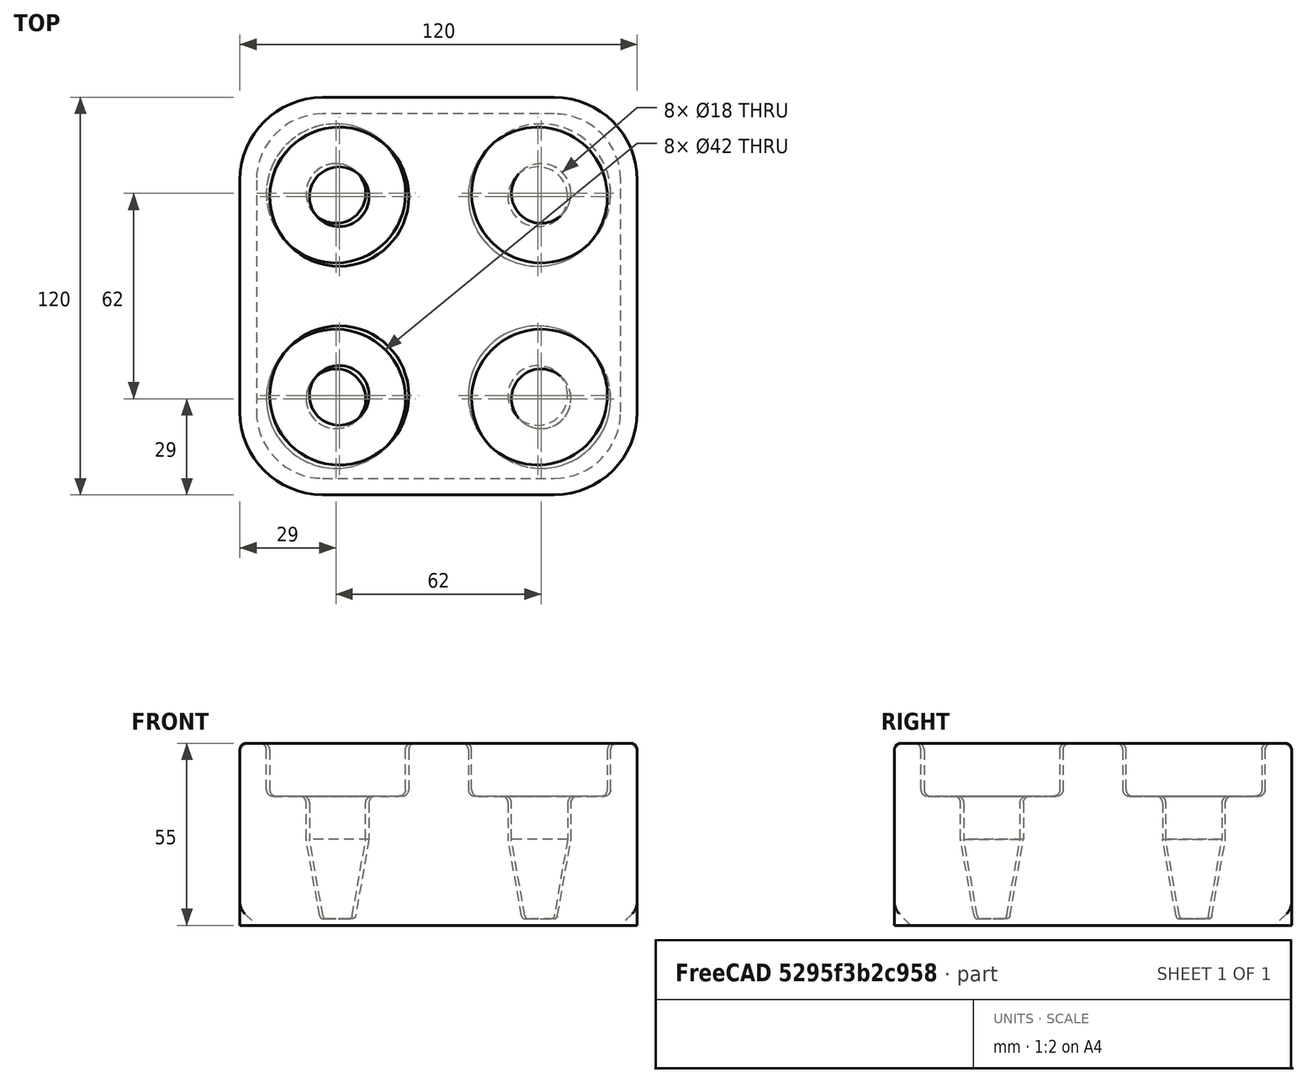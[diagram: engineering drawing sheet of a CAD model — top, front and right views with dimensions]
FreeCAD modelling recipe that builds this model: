
FCSTD DOCUMENT  (FreeCAD 1.0R39285 (Git))
Label: DressingBottleHolder
License: All rights reserved
LicenseURL: https://en.wikipedia.org/wiki/All_rights_reserved
objects: TechDraw::DrawViewDimension×16, Sketcher::SketchObject×7, Part::Part2DObjectPython×4, PartDesign::Body×3, Part::Feature×1, PartDesign::Pad×1, PartDesign::Groove×1, PartDesign::PolarPattern×1, PartDesign::Fillet×1, TechDraw::DrawSVGTemplate×1, TechDraw::DrawProjGroupItem×1, TechDraw::DrawProjGroup×1, TechDraw::DrawComplexSection×1, TechDraw::DrawPage×1
note: 57 computed .brp shape members not serialized (recipe doc carries the construction recipe); baked Part::Feature solids carry a one-line shape summary decoded from their .brp

FEATURE [Part::Feature] Part__Feature  label="2X2 step"
  shape: bbox 124.1 x 124.1 x 55 mm, 70 faces (baked)
FEATURE [Sketcher::SketchObject] Sketch
  ArcFitTolerance = 1e-06
  AttachmentSupport = -> [XY_Plane]
  FullyConstrained = true
  MakeInternals = false
  MapMode = 5
  sketch-geometry (11):
    g0: LineSegment StartX=-60 StartY=35 StartZ=0 EndX=-60 EndY=-35 EndZ=0
    g1: LineSegment StartX=-35 StartY=-60 StartZ=0 EndX=35 EndY=-60 EndZ=0
    g2: LineSegment StartX=60 StartY=-35 StartZ=0 EndX=60 EndY=35 EndZ=0
    g3: LineSegment StartX=35 StartY=60 StartZ=0 EndX=-35 EndY=60 EndZ=0
    g4: ArcOfCircle CenterX=-35 CenterY=35 CenterZ=0 NormalX=0 NormalY=0 NormalZ=1 AngleXU=0 Radius=25 StartAngle=1.5708 EndAngle=3.14159
    g5: ArcOfCircle CenterX=-35 CenterY=-35 CenterZ=0 NormalX=0 NormalY=0 NormalZ=1 AngleXU=0 Radius=25 StartAngle=3.14159 EndAngle=4.71239
    g6: ArcOfCircle CenterX=35 CenterY=-35 CenterZ=0 NormalX=0 NormalY=0 NormalZ=1 AngleXU=0 Radius=25 StartAngle=4.71239 EndAngle=6.28319
    g7: ArcOfCircle CenterX=35 CenterY=35 CenterZ=0 NormalX=0 NormalY=0 NormalZ=1 AngleXU=0 Radius=25 StartAngle=-5.0129e-12 EndAngle=1.5708
    g8: GeomPoint [constr] X=-60 Y=60 Z=0
    g9: GeomPoint [constr] X=60 Y=-60 Z=0
    g10: Circle [constr] CenterX=31 CenterY=31 CenterZ=0 NormalX=0 NormalY=0 NormalZ=1 AngleXU=0 Radius=23
  constraints (25):
    c: Tangent(g0,g4) = -1.5708
    c: Tangent(g0,g5) = -1.5708
    c: Tangent(g1,g5) = -1.5708
    c: Tangent(g1,g6) = -1.5708
    c: Tangent(g2,g6) = -1.5708
    c: Tangent(g2,g7) = -1.5708
    c: Tangent(g3,g7) = -1.5708
    c: Tangent(g3,g4) = -1.5708
    c: Vertical(g0)
    c: Vertical(g2)
    c: Horizontal(g1)
    c: Horizontal(g3)
    c: Equal(g6,g7)
    c: PointOnObject(g8,g0)
    c: PointOnObject(g8,g3)
    c: PointOnObject(g9,g1)
    c: PointOnObject(g9,g2)
    c: Symmetric(g2,g0,g-2)
    c: Symmetric(g1,g3,g-1)
    c: Equal(g0,g3)
    c: DistanceY(g1,g3) = 120
    c: Radius(g7) = 25
    c: DistanceX(g10) = 31
    c: DistanceY(g10) = 31
    c: Diameter(g10) = 46
FEATURE [PartDesign::Pad] Pad
  Direction = (0,0,1)
  Length = 55
  Length2 = 10
  Profile = -> Sketch
  ReferenceAxis = -> Sketch [N_Axis]
  Refine = true
  Suppressed = false
  Type = 0
FEATURE [Sketcher::SketchObject] Sketch001
  ArcFitTolerance = 1e-06
  AttachmentOffset = pos=(31,0,-31) rot=(0,0,1;0rad)
  AttachmentSupport = -> [XZ_Plane]
  ExternalGeometry = -> [Pad]
  FullyConstrained = true
  MakeInternals = false
  MapMode = 5
  Placement = pos=(31,31,-6.9e-15) rot=(1,0,0;1.5708rad)
  expr: Constraints[29] = 2 mm
  expr: Constraints[38] = 26 mm
  sketch-geometry (16):
    g0: LineSegment StartX=0 StartY=55 StartZ=0 EndX=0 EndY=2 EndZ=0
    g1: LineSegment StartX=0 StartY=2 StartZ=0 EndX=3.91552 EndY=2 EndZ=0
    g2: LineSegment StartX=4.9 StartY=2.8245 StartZ=0 EndX=8.96896 EndY=25.649 EndZ=0
    g3: LineSegment StartX=9 StartY=26 StartZ=0 EndX=9 EndY=37 EndZ=0
    g4: LineSegment StartX=11 StartY=39 StartZ=0 EndX=19 EndY=39 EndZ=0
    g5: LineSegment StartX=21 StartY=41 StartZ=0 EndX=21 EndY=53 EndZ=0
    g6: LineSegment StartX=0 StartY=55 StartZ=0 EndX=23 EndY=55 EndZ=0
    g7: ArcOfCircle CenterX=23 CenterY=53 CenterZ=0 NormalX=0 NormalY=0 NormalZ=1 AngleXU=0 Radius=2 StartAngle=1.5708 EndAngle=3.14159
    g8: ArcOfCircle CenterX=19 CenterY=41 CenterZ=0 NormalX=0 NormalY=0 NormalZ=1 AngleXU=0 Radius=2 StartAngle=4.71239 EndAngle=6.28319
    g9: GeomPoint [constr] X=21 Y=39 Z=0
    g10: ArcOfCircle CenterX=11 CenterY=37 CenterZ=0 NormalX=0 NormalY=0 NormalZ=1 AngleXU=0 Radius=2 StartAngle=1.5708 EndAngle=3.14159
    g11: GeomPoint [constr] X=9 Y=39 Z=0
    g12: ArcOfCircle CenterX=7 CenterY=26 CenterZ=0 NormalX=0 NormalY=0 NormalZ=1 AngleXU=0 Radius=2 StartAngle=6.10677 EndAngle=6.28319
    g13: GeomPoint [constr] X=9 Y=25.8231 Z=0
    g14: ArcOfCircle CenterX=3.91552 CenterY=3 CenterZ=0 NormalX=0 NormalY=0 NormalZ=1 AngleXU=0 Radius=1 StartAngle=4.71239 EndAngle=6.10677
    g15: GeomPoint [constr] X=4.75302 Y=2 Z=0
  constraints (40):
    c: Vertical(g0)
    c: Coincident(g0,g1)
    c: Horizontal(g1)
    c: Vertical(g3)
    c: Horizontal(g4)
    c: Vertical(g5)
    c: Coincident(g0,g6)
    c: Horizontal(g6)
    c: Tangent(g7,g5) = 1.5708
    c: Tangent(g7,g6) = 1.5708
    c: PointOnObject(g9,g4)
    c: PointOnObject(g9,g5)
    c: Tangent(g4,g8) = -1.5708
    c: Tangent(g5,g8) = -1.5708
    c: PointOnObject(g11,g3)
    c: PointOnObject(g11,g4)
    c: Tangent(g3,g10) = 1.5708
    c: Tangent(g4,g10) = 1.5708
    c: PointOnObject(g13,g2)
    c: PointOnObject(g13,g3)
    c: Tangent(g2,g12) = -1.5708
    c: Tangent(g3,g12) = -1.5708
    c: PointOnObject(g15,g1)
    c: PointOnObject(g15,g2)
    c: Tangent(g1,g14) = -1.5708
    c: Tangent(g2,g14) = -1.5708
    c: Equal(g7,g8)
    c: Equal(g8,g10)
    c: Radius(g7) = 2
    c: DistanceY(g0) = 2
    c: Radius(g14) = 1
    c: DistanceY(g11) = 39
    c: PointOnObject(g6,g-3)
    c: DistanceX(g0,g5) = 21
    c: DistanceX(g0,g3) = 9
    c: DistanceX(g0,g2) = 4.9
    c: Equal(g12,g10)
    c: PointOnObject(g0,g-2)
    c: DistanceY(g3) = 26
    c: DistanceX(g6) = 23
FEATURE [PartDesign::Groove] Groove
  Angle = 360
  Angle2 = 60
  Axis = (0,2e-16,1)
  Base = (31,31,-6.9e-15)
  BaseFeature = -> Pad
  Profile = -> Sketch001
  ReferenceAxis = -> Sketch001 [V_Axis]
  Refine = true
  Suppressed = false
  Type = 0
FEATURE [PartDesign::PolarPattern] PolarPattern
  Angle = 360
  Axis = -> Z_Axis
  BaseFeature = -> Groove
  Mode = 0
  Occurrences = 4
  Offset = 120
  Originals = -> [Groove]
  Refine = true
  Suppressed = false
  TransformMode = 0
FEATURE [PartDesign::Fillet] Fillet
  Base = -> PolarPattern [Edge20]
  BaseFeature = -> PolarPattern
  Radius = 2
  Refine = true
  SupportTransform = false
  Suppressed = false
  UseAllEdges = false
FEATURE [TechDraw::DrawSVGTemplate] Template
  Height = 297
  Orientation = 0
  Template = <path>
  Width = 210
FEATURE [Sketcher::SketchObject] Sketch002
  ArcFitTolerance = 1e-06
  AttachmentSupport = -> [Fillet]
  FullyConstrained = false
  MakeInternals = false
  MapMode = 5
  Placement = pos=(0,0,55) rot=(0,0,1;0rad)
  sketch-geometry (3):
    g0: LineSegment StartX=-75.5453 StartY=0 StartZ=0 EndX=0 EndY=0 EndZ=0
    g1: LineSegment StartX=0 StartY=0 StartZ=0 EndX=0 EndY=31 EndZ=0
    g2: LineSegment StartX=0 StartY=31 StartZ=0 EndX=79.1188 EndY=31 EndZ=0
  constraints (7):
    c: PointOnObject(g0,g-1)
    c: Coincident(g0,g-1)
    c: Coincident(g0,g1)
    c: PointOnObject(g1,g-2)
    c: Coincident(g1,g2)
    c: Horizontal(g2)
    c: DistanceY(g1,g1) = 31
FEATURE [PartDesign::Body] Body  label="2x2"
  AllowCompound = false
  Group = -> [Sketch,Sketch001,Pad,Groove,PolarPattern,Fillet,Sketch002]
  Origin = -> Origin
  Tip = -> Fillet
FEATURE [TechDraw::DrawProjGroupItem] ProjItem  label="Top"
  CoarseView = false
  Direction = (0,0,1)
  Focus = 100
  HardHidden = false
  IsoCount = 0
  IsoHidden = false
  IsoVisible = false
  LockPosition = true
  Perspective = false
  Rotation = 0
  RotationVector = (1,0,0)
  ScaleType = 0
  ScrubCount = 1
  SeamHidden = false
  SeamVisible = false
  SmoothHidden = false
  SmoothVisible = true
  Source = -> [Body]
  Type = 0
  X = 0
  XDirection = (1,0,0)
  Y = 0
FEATURE [TechDraw::DrawProjGroup] ProjGroup
  Anchor = -> ProjItem
  AutoDistribute = true
  LockPosition = false
  ProjectionType = 0
  Rotation = 0
  ScaleType = 0
  Source = -> [Body]
  Views = -> [ProjItem]
  X = 110.819
  Y = 78.5207
  spacingX = 15
  spacingY = 15
FEATURE [TechDraw::DrawViewDimension] Dimension
  AngleOverride = false
  Arbitrary = false
  ArbitraryTolerances = false
  BoxCorners = (2) [(-60,-60,-1e-07),(60,60,1e-07)]
  EqualTolerance = true
  ExtensionAngle = 0
  FormatSpec = %.2w
  FormatSpecOverTolerance = %+.2w
  FormatSpecUnderTolerance = %+.2w
  Inverted = false
  LineAngle = 0
  LockPosition = false
  MeasureType = 1
  OverTolerance = 0
  References2D = -> [ProjItem]
  Rotation = 0
  ScaleType = 0
  TheoreticalExact = false
  Type = 1
  UnderTolerance = 0
  X = 0
  Y = 92.7629
FEATURE [TechDraw::DrawViewDimension] Dimension001
  AngleOverride = false
  Arbitrary = false
  ArbitraryTolerances = false
  BoxCorners = (2) [(-60,-60,-1e-07),(60,60,1e-07)]
  EqualTolerance = true
  ExtensionAngle = 0
  FormatSpec = %.2w
  FormatSpecOverTolerance = %+.2w
  FormatSpecUnderTolerance = %+.2w
  Inverted = false
  LineAngle = 0
  LockPosition = false
  MeasureType = 1
  OverTolerance = 0
  References2D = -> [ProjItem]
  Rotation = 0
  ScaleType = 0
  TheoreticalExact = false
  Type = 2
  UnderTolerance = 0
  X = -105.136
  Y = 0
FEATURE [TechDraw::DrawViewDimension] Dimension002
  AngleOverride = false
  Arbitrary = false
  ArbitraryTolerances = false
  BoxCorners = (2) [(-60,-60,-1e-07),(60,60,1e-07)]
  EqualTolerance = true
  ExtensionAngle = 0
  FormatSpec = R%.2w
  FormatSpecOverTolerance = %+.2w
  FormatSpecUnderTolerance = %+.2w
  Inverted = false
  LineAngle = 0
  LockPosition = false
  MeasureType = 1
  OverTolerance = 0
  References2D = -> [ProjItem]
  Rotation = 0
  ScaleType = 0
  TheoreticalExact = false
  Type = 4
  UnderTolerance = 0
  X = 70.8117
  Y = -52.3925
FEATURE [TechDraw::DrawComplexSection] ComplexSection  label="Section A - A"
  BaseView = -> ProjItem
  CoarseView = false
  CutSurfaceDisplay = 2
  CuttingToolWireObject = -> Sketch002
  Direction = (1e-16,-1,0)
  FileGeomPattern = <path>
  FileHatchPattern = <path>
  Focus = 100
  FuseBeforeCut = false
  HardHidden = false
  HatchOffset = (0,0,0)
  HatchRotation = 0
  HatchScale = 1
  IsoCount = 0
  IsoHidden = false
  IsoVisible = false
  LockPosition = false
  NameGeomPattern = Diamond
  Perspective = false
  ProjectionStrategy = 0
  Rotation = 0
  ScaleType = 0
  ScrubCount = 1
  SeamHidden = false
  SeamVisible = false
  SectionDirection = 4
  SectionLineStretch = 1
  SectionNormal = (1e-16,-1,0)
  SectionOrigin = (0,0,0)
  SectionSymbol = A
  SmoothHidden = false
  SmoothVisible = true
  Source = -> [Body]
  TrimAfterCut = false
  UsePreviousCut = false
  X = 110.819
  XDirection = (1,1e-16,0)
  Y = 208.194
FEATURE [TechDraw::DrawViewDimension] Dimension003
  AngleOverride = false
  Arbitrary = false
  ArbitraryTolerances = false
  BoxCorners = (2) [(-60,-27.5,-1e-07),(60,27.5,1e-07)]
  EqualTolerance = true
  ExtensionAngle = 0
  FormatSpec = %.2w
  FormatSpecOverTolerance = %+.2w
  FormatSpecUnderTolerance = %+.2w
  Inverted = false
  LineAngle = 0
  LockPosition = false
  MeasureType = 1
  OverTolerance = 0
  References2D = -> [ComplexSection]
  Rotation = 0
  ScaleType = 0
  TheoreticalExact = false
  Type = 2
  UnderTolerance = 0
  X = -76.9265
  Y = -30.5684
FEATURE [TechDraw::DrawViewDimension] Dimension005
  AngleOverride = false
  Arbitrary = false
  ArbitraryTolerances = false
  BoxCorners = (2) [(-60,-27.5,-1e-07),(60,27.5,1e-07)]
  EqualTolerance = true
  ExtensionAngle = 0
  FormatSpec = %.2w
  FormatSpecOverTolerance = %+.2w
  FormatSpecUnderTolerance = %+.2w
  Inverted = false
  LineAngle = 0
  LockPosition = false
  MeasureType = 1
  OverTolerance = 0
  References2D = -> [ComplexSection]
  Rotation = 0
  ScaleType = 0
  TheoreticalExact = false
  Type = 2
  UnderTolerance = 0
  X = -83.9265
  Y = 19.5
FEATURE [TechDraw::DrawViewDimension] Dimension006
  AngleOverride = false
  Arbitrary = false
  ArbitraryTolerances = false
  BoxCorners = (2) [(-60,-27.5,-1e-07),(60,27.5,1e-07)]
  EqualTolerance = true
  ExtensionAngle = 0
  FormatSpec = %.2w
  FormatSpecOverTolerance = %+.2w
  FormatSpecUnderTolerance = %+.2w
  Inverted = false
  LineAngle = 0
  LockPosition = false
  MeasureType = 1
  OverTolerance = 0
  References2D = -> [ComplexSection]
  Rotation = 0
  ScaleType = 0
  TheoreticalExact = false
  Type = 1
  UnderTolerance = 0
  X = 66.5034
  Y = 65.1724
FEATURE [TechDraw::DrawViewDimension] Dimension007
  AngleOverride = false
  Arbitrary = false
  ArbitraryTolerances = false
  BoxCorners = (2) [(-60,-27.5,-1e-07),(60,27.5,1e-07)]
  EqualTolerance = true
  ExtensionAngle = 0
  FormatSpec = %.2w
  FormatSpecOverTolerance = %+.2w
  FormatSpecUnderTolerance = %+.2w
  Inverted = false
  LineAngle = 0
  LockPosition = false
  MeasureType = 1
  OverTolerance = 0
  References2D = -> [ComplexSection]
  Rotation = 0
  ScaleType = 0
  TheoreticalExact = false
  Type = 1
  UnderTolerance = 0
  X = 65.5931
  Y = 53.7241
FEATURE [TechDraw::DrawViewDimension] Dimension008
  AngleOverride = false
  Arbitrary = false
  ArbitraryTolerances = false
  BoxCorners = (2) [(-60,-27.5,-1e-07),(60,27.5,1e-07)]
  EqualTolerance = true
  ExtensionAngle = 0
  FormatSpec = %.2w
  FormatSpecOverTolerance = %+.2w
  FormatSpecUnderTolerance = %+.2w
  Inverted = false
  LineAngle = 0
  LockPosition = false
  MeasureType = 1
  OverTolerance = 0
  References2D = -> [ComplexSection]
  Rotation = 0
  ScaleType = 0
  TheoreticalExact = false
  Type = 1
  UnderTolerance = 0
  X = 64.8345
  Y = 42.1568
FEATURE [TechDraw::DrawViewDimension] Dimension009
  AngleOverride = false
  Arbitrary = false
  ArbitraryTolerances = false
  BoxCorners = (2) [(-60,-27.5,-1e-07),(60,27.5,1e-07)]
  EqualTolerance = true
  ExtensionAngle = 0
  FormatSpec = R%.2w
  FormatSpecOverTolerance = %+.2w
  FormatSpecUnderTolerance = %+.2w
  Inverted = false
  LineAngle = 0
  LockPosition = false
  MeasureType = 1
  OverTolerance = 0
  References2D = -> [ComplexSection]
  Rotation = 0
  ScaleType = 0
  TheoreticalExact = false
  Type = 4
  UnderTolerance = 0
  X = 1.67471
  Y = 41.3096
FEATURE [TechDraw::DrawViewDimension] Dimension010
  AngleOverride = false
  Arbitrary = false
  ArbitraryTolerances = false
  BoxCorners = (2) [(-60,-27.5,-1e-07),(60,27.5,1e-07)]
  EqualTolerance = true
  ExtensionAngle = 0
  FormatSpec = R%.2w
  FormatSpecOverTolerance = %+.2w
  FormatSpecUnderTolerance = %+.2w
  Inverted = false
  LineAngle = 0
  LockPosition = false
  MeasureType = 1
  OverTolerance = 0
  References2D = -> [ComplexSection]
  Rotation = 0
  ScaleType = 0
  TheoreticalExact = false
  Type = 4
  UnderTolerance = 0
  X = -22.82
  Y = 42.3106
FEATURE [TechDraw::DrawViewDimension] Dimension011
  AngleOverride = false
  Arbitrary = false
  ArbitraryTolerances = false
  BoxCorners = (2) [(-60,-27.5,-1e-07),(60,27.5,1e-07)]
  EqualTolerance = true
  ExtensionAngle = 0
  FormatSpec = R%.2w
  FormatSpecOverTolerance = %+.2w
  FormatSpecUnderTolerance = %+.2w
  Inverted = false
  LineAngle = 0
  LockPosition = false
  MeasureType = 1
  OverTolerance = 0
  References2D = -> [ComplexSection]
  Rotation = 0
  ScaleType = 0
  TheoreticalExact = false
  Type = 4
  UnderTolerance = 0
  X = -43.195
  Y = 40.1492
FEATURE [TechDraw::DrawViewDimension] Dimension013
  AngleOverride = false
  Arbitrary = false
  ArbitraryTolerances = false
  BoxCorners = (2) [(-60,-27.5,-1e-07),(60,27.5,1e-07)]
  EqualTolerance = true
  ExtensionAngle = 0
  FormatSpec = %.2w
  FormatSpecOverTolerance = %+.2w
  FormatSpecUnderTolerance = %+.2w
  Inverted = false
  LineAngle = 0
  LockPosition = false
  MeasureType = 1
  OverTolerance = 0
  References2D = -> [ComplexSection]
  Rotation = 0
  ScaleType = 0
  TheoreticalExact = false
  Type = 2
  UnderTolerance = 0
  X = -83.9265
  Y = -10.1099
FEATURE [TechDraw::DrawViewDimension] Dimension014
  AngleOverride = false
  Arbitrary = false
  ArbitraryTolerances = false
  BoxCorners = (2) [(-60,-27.5,-1e-07),(60,27.5,1e-07)]
  EqualTolerance = true
  ExtensionAngle = 0
  FormatSpec = %.2w
  FormatSpecOverTolerance = %+.2w
  FormatSpecUnderTolerance = %+.2w
  Inverted = false
  LineAngle = 0
  LockPosition = false
  MeasureType = 1
  OverTolerance = 0
  References2D = -> [ComplexSection]
  Rotation = 0
  ScaleType = 0
  TheoreticalExact = false
  Type = 2
  UnderTolerance = 0
  X = -83.9265
  Y = 5
FEATURE [TechDraw::DrawViewDimension] Dimension015
  AngleOverride = false
  Arbitrary = false
  ArbitraryTolerances = false
  BoxCorners = (2) [(-60,-60,-1e-07),(60,60,1e-07)]
  EqualTolerance = true
  ExtensionAngle = 0
  FormatSpec = %.2w
  FormatSpecOverTolerance = %+.2w
  FormatSpecUnderTolerance = %+.2w
  Inverted = false
  LineAngle = 0
  LockPosition = false
  MeasureType = 1
  OverTolerance = 0
  References2D = -> [ProjItem]
  Rotation = 0
  ScaleType = 0
  TheoreticalExact = false
  Type = 1
  UnderTolerance = 0
  X = 15.5
  Y = 75.1201
FEATURE [TechDraw::DrawViewDimension] Dimension016
  AngleOverride = false
  Arbitrary = false
  ArbitraryTolerances = false
  BoxCorners = (2) [(-60,-60,-1e-07),(60,60,1e-07)]
  EqualTolerance = true
  ExtensionAngle = 0
  FormatSpec = %.2w
  FormatSpecOverTolerance = %+.2w
  FormatSpecUnderTolerance = %+.2w
  Inverted = false
  LineAngle = 0
  LockPosition = false
  MeasureType = 1
  OverTolerance = 0
  References2D = -> [ProjItem]
  Rotation = 0
  ScaleType = 0
  TheoreticalExact = false
  Type = 2
  UnderTolerance = 0
  X = -92.8089
  Y = 15.5
FEATURE [TechDraw::DrawViewDimension] Dimension017
  AngleOverride = false
  Arbitrary = false
  ArbitraryTolerances = false
  BoxCorners = (2) [(-60,-27.5,-1e-07),(60,27.5,1e-07)]
  EqualTolerance = true
  ExtensionAngle = 0
  FormatSpec = R%.2w
  FormatSpecOverTolerance = %+.2w
  FormatSpecUnderTolerance = %+.2w
  Inverted = false
  LineAngle = 0
  LockPosition = false
  MeasureType = 1
  OverTolerance = 0
  References2D = -> [ComplexSection]
  Rotation = 0
  ScaleType = 0
  TheoreticalExact = false
  Type = 4
  UnderTolerance = 0
  X = -65.9067
  Y = 41.2738
FEATURE [TechDraw::DrawPage] Page
  KeepUpdated = true
  NextBalloonIndex = 1
  ProjectionType = 0
  Template = -> Template
  Views = -> [ProjGroup,Dimension,Dimension001,Dimension002,ComplexSection,Dimension003,Dimension005,Dimension006,Dimension007,Dimension008,Dimension009,Dimension010,Dimension011,Dimension013,Dimension014,Dimension015,Dimension016,Dimension017]
FEATURE [Sketcher::SketchObject] Sketch003  label="1x1"
  ArcFitTolerance = 1e-06
  AttachmentSupport = -> [XY_Plane001]
  FullyConstrained = true
  MakeInternals = false
  MapMode = 5
  sketch-geometry (12):
    g0: Circle CenterX=0 CenterY=0 CenterZ=0 NormalX=0 NormalY=0 NormalZ=1 AngleXU=0 Radius=23
    g1: LineSegment StartX=-30.5 StartY=22.5 StartZ=0 EndX=-30.5 EndY=-22.5 EndZ=0
    g2: LineSegment StartX=-22.5 StartY=-30.5 StartZ=0 EndX=22.5 EndY=-30.5 EndZ=0
    g3: LineSegment StartX=30.5 StartY=-22.5 StartZ=0 EndX=30.5 EndY=22.5 EndZ=0
    g4: LineSegment StartX=22.5 StartY=30.5 StartZ=0 EndX=-22.5 EndY=30.5 EndZ=0
    g5: ArcOfCircle CenterX=-22.5 CenterY=22.5 CenterZ=0 NormalX=0 NormalY=0 NormalZ=1 AngleXU=0 Radius=8 StartAngle=1.5708 EndAngle=3.14159
    g6: ArcOfCircle CenterX=-22.5 CenterY=-22.5 CenterZ=0 NormalX=0 NormalY=0 NormalZ=1 AngleXU=0 Radius=8 StartAngle=3.14159 EndAngle=4.71239
    g7: ArcOfCircle CenterX=22.5 CenterY=-22.5 CenterZ=0 NormalX=0 NormalY=0 NormalZ=1 AngleXU=0 Radius=8 StartAngle=4.71239 EndAngle=6.28319
    g8: ArcOfCircle CenterX=22.5 CenterY=22.5 CenterZ=0 NormalX=0 NormalY=0 NormalZ=1 AngleXU=0 Radius=8 StartAngle=0 EndAngle=1.5708
    g9: GeomPoint [constr] X=-30.5 Y=30.5 Z=0
    g10: GeomPoint [constr] X=30.5 Y=-30.5 Z=0
    g11: Circle CenterX=0 CenterY=0 CenterZ=0 NormalX=0 NormalY=0 NormalZ=1 AngleXU=0 Radius=28.5
  constraints (28):
    c: Diameter(g0) = 46
    c: Coincident(g0,g-1)
    c: Tangent(g1,g5) = -1.5708
    c: Tangent(g1,g6) = -1.5708
    c: Tangent(g2,g6) = -1.5708
    c: Tangent(g2,g7) = -1.5708
    c: Tangent(g3,g7) = -1.5708
    c: Tangent(g3,g8) = -1.5708
    c: Tangent(g4,g8) = -1.5708
    c: Tangent(g4,g5) = -1.5708
    c: Vertical(g1)
    c: Vertical(g3)
    c: Horizontal(g2)
    c: Horizontal(g4)
    c: Equal(g6,g7)
    c: PointOnObject(g9,g1)
    c: PointOnObject(g9,g4)
    c: PointOnObject(g10,g2)
    c: PointOnObject(g10,g3)
    c: Symmetric(g3,g1,g-2)
    c: Symmetric(g4,g2,g-1)
    c: Equal(g1,g4)
    c: Radius(g7) = 8
    c: Diameter(g11) = 57
    c: Coincident(g11,g0)
    c: Distance(g11,g1) = 2
    c: DistanceX(g1,g3) = 61
    c: Distance(g0,g1) = 7.5
FEATURE [Sketcher::SketchObject] Sketch004  label="Hole Profile"
  ArcFitTolerance = 1e-06
  AttachmentSupport = -> [XZ_Plane001]
  FullyConstrained = true
  MakeInternals = false
  MapMode = 5
  Placement = pos=(0,0,0) rot=(1,0,0;1.5708rad)
  sketch-geometry (16):
    g0: LineSegment StartX=-23 StartY=0 StartZ=0 EndX=-23 EndY=-53 EndZ=0
    g1: LineSegment StartX=-23 StartY=-53 StartZ=0 EndX=-19.0845 EndY=-53 EndZ=0
    g2: LineSegment StartX=-18.1 StartY=-52.1755 StartZ=0 EndX=-14.031 EndY=-29.35 EndZ=0
    g3: LineSegment StartX=-14 StartY=-28.999 StartZ=0 EndX=-14 EndY=-18 EndZ=0
    g4: LineSegment StartX=-12 StartY=-16 StartZ=0 EndX=-4 EndY=-16 EndZ=0
    g5: LineSegment StartX=-2 StartY=-14 StartZ=0 EndX=-2 EndY=-2 EndZ=0
    g6: LineSegment StartX=-23 StartY=0 StartZ=0 EndX=0 EndY=0 EndZ=0
    g7: ArcOfCircle CenterX=-1.2e-15 CenterY=-2 CenterZ=0 NormalX=0 NormalY=0 NormalZ=1 AngleXU=0 Radius=2 StartAngle=1.5708 EndAngle=3.14159
    g8: ArcOfCircle CenterX=-4 CenterY=-14 CenterZ=0 NormalX=0 NormalY=0 NormalZ=1 AngleXU=0 Radius=2 StartAngle=4.71239 EndAngle=6.28319
    g9: GeomPoint [constr] X=-2 Y=-16 Z=0
    g10: ArcOfCircle CenterX=-12 CenterY=-18 CenterZ=0 NormalX=0 NormalY=0 NormalZ=1 AngleXU=0 Radius=2 StartAngle=1.5708 EndAngle=3.14159
    g11: GeomPoint [constr] X=-14 Y=-16 Z=0
    g12: ArcOfCircle CenterX=-16 CenterY=-28.999 CenterZ=0 NormalX=0 NormalY=0 NormalZ=1 AngleXU=0 Radius=2 StartAngle=6.10677 EndAngle=6.28319
    g13: GeomPoint [constr] X=-14 Y=-29.1759 Z=0
    g14: ArcOfCircle CenterX=-19.0845 CenterY=-52 CenterZ=0 NormalX=0 NormalY=0 NormalZ=1 AngleXU=0 Radius=1 StartAngle=4.71239 EndAngle=6.10677
    g15: GeomPoint [constr] X=-18.247 Y=-53 Z=0
  constraints (38):
    c: Vertical(g0)
    c: Coincident(g0,g1)
    c: Horizontal(g1)
    c: Vertical(g3)
    c: Horizontal(g4)
    c: Vertical(g5)
    c: Coincident(g0,g6)
    c: Horizontal(g6)
    c: Tangent(g7,g5) = 1.5708
    c: Tangent(g7,g6) = 1.5708
    c: PointOnObject(g9,g4)
    c: PointOnObject(g9,g5)
    c: Tangent(g4,g8) = -1.5708
    c: Tangent(g5,g8) = -1.5708
    c: PointOnObject(g11,g3)
    c: PointOnObject(g11,g4)
    c: Tangent(g3,g10) = 1.5708
    c: Tangent(g4,g10) = 1.5708
    c: PointOnObject(g13,g2)
    c: PointOnObject(g13,g3)
    c: Tangent(g2,g12) = -1.5708
    c: Tangent(g3,g12) = -1.5708
    c: PointOnObject(g15,g1)
    c: PointOnObject(g15,g2)
    c: Tangent(g1,g14) = -1.5708
    c: Tangent(g2,g14) = -1.5708
    c: Equal(g7,g8)
    c: Equal(g8,g10)
    c: Radius(g7) = 2
    c: Radius(g14) = 1
    c: DistanceX(g0,g5) = 21
    c: DistanceX(g0,g3) = 9
    c: DistanceX(g0,g2) = 4.9
    c: Equal(g12,g10)
    c: DistanceY(g0,g0) = 53
    c: DistanceY(g0,g2) = 23.65
    c: DistanceY(g0,g4) = 37
    c: Coincident(g6,g-1)
FEATURE [Sketcher::SketchObject] Sketch005  label="Spout"
  ArcFitTolerance = 1e-06
  AttachmentSupport = -> [XZ_Plane002]
  FullyConstrained = true
  MakeInternals = false
  MapMode = 5
  Placement = pos=(0,0,0) rot=(1,0,0;1.5708rad)
  sketch-geometry (15):
    g0: LineSegment StartX=-49 StartY=20 StartZ=0 EndX=-49 EndY=-3.6e-15 EndZ=0
    g1: LineSegment StartX=-49 StartY=-2.2e-15 StartZ=0 EndX=-44 EndY=-2.2e-15 EndZ=0
    g2: LineSegment StartX=-44 StartY=-2.2e-15 StartZ=0 EndX=-44 EndY=-18 EndZ=0
    g3: LineSegment StartX=-44 StartY=-18 StartZ=0 EndX=-34 EndY=-18 EndZ=0
    g4: LineSegment StartX=-29 StartY=-51 StartZ=0 EndX=-17 EndY=-51 EndZ=0
    g5: LineSegment StartX=-12 StartY=-18 StartZ=0 EndX=-2 EndY=-18 EndZ=0
    g6: LineSegment StartX=-2 StartY=-18 StartZ=0 EndX=-2 EndY=0 EndZ=0
    g7: LineSegment StartX=-2 StartY=0 StartZ=0 EndX=3 EndY=0 EndZ=0
    g8: LineSegment StartX=3 StartY=0 StartZ=0 EndX=3 EndY=20 EndZ=0
    g9: LineSegment StartX=-23 StartY=-51 StartZ=0 EndX=-23 EndY=20 EndZ=0
    g10: LineSegment [constr] StartX=0 StartY=0 StartZ=0 EndX=-46 EndY=0 EndZ=0
    g11: LineSegment StartX=-12 StartY=-18 StartZ=0 EndX=-12 EndY=-29 EndZ=0
    g12: LineSegment StartX=-12 StartY=-29 StartZ=0 EndX=-17 EndY=-51 EndZ=0
    g13: LineSegment StartX=-34 StartY=-18 StartZ=0 EndX=-34 EndY=-29 EndZ=0
    g14: LineSegment StartX=-34 StartY=-29 StartZ=0 EndX=-29 EndY=-51 EndZ=0
  constraints (48):
    c: Vertical(g0)
    c: Coincident(g0,g1)
    c: Horizontal(g1)
    c: Coincident(g1,g2)
    c: Vertical(g2)
    c: Coincident(g2,g3)
    c: Horizontal(g3)
    c: Horizontal(g4)
    c: Horizontal(g5)
    c: Coincident(g5,g6)
    c: Vertical(g6)
    c: Coincident(g7,g8)
    c: Vertical(g8)
    c: Horizontal(g7)
    c: Equal(g0,g8)
    c: Equal(g7,g1)
    c: Equal(g2,g6)
    c: Equal(g5,g3)
    c: DistanceX(g4,g4) = 12
    c: DistanceX(g3,g5) = 22
    c: Horizontal(g8,g0)
    c: DistanceY(g5,g7) = 18
    c: DistanceY(g4,g7) = 51
    c: DistanceY(g7,g8) = 20
    c: Coincident(g7,g6)
    c: PointOnObject(g6,g-1)
    c: DistanceX(g6,g-1) = 2
    c: Symmetric(g4,g4,g9)
    c: Vertical(g9)
    c: Horizontal(g9,g8)
    c: DistanceX(g2,g5) = 42
    c: DistanceX(g0,g7) = 52
    c: Coincident(g10,g-1)
    c: Symmetric(g10,g10,g9)
    c: DistanceX(g10,g10) = 46
    c: Coincident(g5,g11)
    c: Vertical(g11)
    c: Coincident(g11,g12)
    c: Coincident(g12,g4)
    c: Coincident(g3,g13)
    c: Vertical(g13)
    c: Coincident(g13,g14)
    c: Coincident(g14,g4)
    c: Equal(g11,g13)
    c: DistanceY(g4,g11) = 22
    c: DistanceY(g11,g5) = 11
    c: Equal(g12,g14)
    c: DistanceY(g11,g7) = 29
FEATURE [Part::Part2DObjectPython] Wire  # Draft 2D object (typed FeaturePython)
  Area = 144.5
  ChamferSize = 0
  Closed = true
  End = (0,0,-20)
  FilletRadius = 0
  Length = 140.096
  MakeFace = true
  Placement = pos=(0,0,0) rot=(1,0,0;1.5708rad)
  Points = (17) [(0,0,0),(-2,-2,-4.44089e-16),(-2,-18,-3.9968e-15),(-4,-20,-4.44089e-15),(-11,-20,-4.44089e-15),(-13,-22,-4.88498e-15),(-17,-51,-1.13243e-14),+10 more]
  Start = (0,0,0)
  Subdivisions = 0
FEATURE [PartDesign::Body] Body002  label="Hole Profile002"
  AllowCompound = false
  Group = -> [Sketch005,Wire]
  Origin = -> Origin002
FEATURE [Sketcher::SketchObject] Sketch006
  ArcFitTolerance = 1e-06
  AttachmentSupport = -> [XY_Plane001]
  FullyConstrained = true
  MakeInternals = false
  MapMode = 5
  sketch-geometry (36):
    g0: Circle CenterX=33 CenterY=33 CenterZ=0 NormalX=0 NormalY=0 NormalZ=1 AngleXU=0 Radius=28.5
    g1: Circle CenterX=95 CenterY=33 CenterZ=0 NormalX=0 NormalY=0 NormalZ=1 AngleXU=0 Radius=28.5
    g2: Circle CenterX=33 CenterY=95 CenterZ=0 NormalX=0 NormalY=0 NormalZ=1 AngleXU=0 Radius=28.5
    g3: Circle CenterX=95 CenterY=95 CenterZ=0 NormalX=0 NormalY=0 NormalZ=1 AngleXU=0 Radius=28.5
    g4: LineSegment StartX=0 StartY=122 StartZ=0 EndX=0 EndY=6 EndZ=0
    g5: LineSegment StartX=6 StartY=0 StartZ=0 EndX=122 EndY=0 EndZ=0
    g6: LineSegment StartX=128 StartY=6 StartZ=0 EndX=128 EndY=122 EndZ=0
    g7: LineSegment StartX=122 StartY=128 StartZ=0 EndX=6 EndY=128 EndZ=0
    g8: ArcOfCircle CenterX=6 CenterY=122 CenterZ=0 NormalX=0 NormalY=0 NormalZ=1 AngleXU=0 Radius=6 StartAngle=1.5708 EndAngle=3.14159
    g9: ArcOfCircle CenterX=6 CenterY=6 CenterZ=0 NormalX=0 NormalY=0 NormalZ=1 AngleXU=0 Radius=6 StartAngle=3.14159 EndAngle=4.71239
    g10: ArcOfCircle CenterX=122 CenterY=6 CenterZ=0 NormalX=0 NormalY=0 NormalZ=1 AngleXU=0 Radius=6 StartAngle=4.71239 EndAngle=6.28319
    g11: ArcOfCircle CenterX=122 CenterY=122 CenterZ=0 NormalX=0 NormalY=0 NormalZ=1 AngleXU=0 Radius=6 StartAngle=1e-16 EndAngle=1.5708
    g12: GeomPoint [constr] X=0 Y=128 Z=0
    g13: GeomPoint [constr] X=128 Y=0 Z=0
    g14: LineSegment StartX=0 StartY=60 StartZ=0 EndX=0 EndY=6 EndZ=0
    g15: LineSegment StartX=6 StartY=0 StartZ=0 EndX=60 EndY=0 EndZ=0
    g16: LineSegment StartX=66 StartY=6 StartZ=0 EndX=66 EndY=60 EndZ=0
    g17: LineSegment StartX=60 StartY=66 StartZ=0 EndX=6 EndY=66 EndZ=0
    g18: ArcOfCircle CenterX=6 CenterY=60 CenterZ=0 NormalX=0 NormalY=0 NormalZ=1 AngleXU=0 Radius=6 StartAngle=1.5708 EndAngle=3.14159
    g19: ArcOfCircle CenterX=6 CenterY=6 CenterZ=0 NormalX=0 NormalY=0 NormalZ=1 AngleXU=0 Radius=6 StartAngle=3.14159 EndAngle=4.71239
    g20: ArcOfCircle CenterX=60 CenterY=6 CenterZ=0 NormalX=0 NormalY=0 NormalZ=1 AngleXU=0 Radius=6 StartAngle=4.71239 EndAngle=6.28319
    g21: ArcOfCircle CenterX=60 CenterY=60 CenterZ=0 NormalX=0 NormalY=0 NormalZ=1 AngleXU=0 Radius=6 StartAngle=5e-16 EndAngle=1.5708
    g22: GeomPoint [constr] X=0 Y=66 Z=0
    g23: GeomPoint [constr] X=66 Y=0 Z=0
    g24: LineSegment StartX=0 StartY=184 StartZ=0 EndX=0 EndY=6 EndZ=0
    g25: LineSegment StartX=6 StartY=0 StartZ=0 EndX=184 EndY=0 EndZ=0
    g26: LineSegment StartX=190 StartY=6 StartZ=0 EndX=190 EndY=184 EndZ=0
    g27: LineSegment StartX=184 StartY=190 StartZ=0 EndX=6 EndY=190 EndZ=0
    g28: ArcOfCircle CenterX=6 CenterY=184 CenterZ=0 NormalX=0 NormalY=0 NormalZ=1 AngleXU=0 Radius=6 StartAngle=1.5708 EndAngle=3.14159
    g29: ArcOfCircle CenterX=6 CenterY=6 CenterZ=0 NormalX=0 NormalY=0 NormalZ=1 AngleXU=0 Radius=6 StartAngle=3.14159 EndAngle=4.71239
    g30: ArcOfCircle CenterX=184 CenterY=6 CenterZ=0 NormalX=0 NormalY=0 NormalZ=1 AngleXU=0 Radius=6 StartAngle=4.71239 EndAngle=6.28319
    g31: ArcOfCircle CenterX=184 CenterY=184 CenterZ=0 NormalX=0 NormalY=0 NormalZ=1 AngleXU=0 Radius=6 StartAngle=1e-15 EndAngle=1.5708
    g32: GeomPoint [constr] X=0 Y=190 Z=0
    g33: GeomPoint [constr] X=190 Y=0 Z=0
    g34: Circle CenterX=33 CenterY=157 CenterZ=0 NormalX=0 NormalY=0 NormalZ=1 AngleXU=0 Radius=28.5
    g35: Circle CenterX=157 CenterY=33 CenterZ=0 NormalX=0 NormalY=0 NormalZ=1 AngleXU=0 Radius=28.5
  constraints (97):
    c: Equal(g1,g0)
    c: Equal(g0,g2)
    c: Equal(g2,g3)
    c: Horizontal(g0,g1)
    c: Horizontal(g2,g3)
    c: Vertical(g0,g2)
    c: Vertical(g1,g3)
    c: Tangent(g4,g8) = -1.5708
    c: Tangent(g4,g9) = -1.5708
    c: Tangent(g5,g9) = -1.5708
    c: Tangent(g5,g10) = -1.5708
    c: Tangent(g6,g10) = -1.5708
    c: Tangent(g6,g11) = -1.5708
    c: Tangent(g7,g11) = -1.5708
    c: Tangent(g7,g8) = -1.5708
    c: Vertical(g4)
    c: Vertical(g6)
    c: Horizontal(g5)
    c: Horizontal(g7)
    c: Equal(g8,g9)
    c: Equal(g9,g10)
    c: Equal(g10,g11)
    c: PointOnObject(g12,g4)
    c: PointOnObject(g12,g7)
    c: PointOnObject(g13,g5)
    c: PointOnObject(g13,g6)
    c: Radius(g9) = 6
    c: Equal(g6,g7)
    c: PointOnObject(g5,g-1)
    c: PointOnObject(g4,g-2)
    c: Diameter(g1) = 57
    c: Distance(g0,g4) = 4.5
    c: Distance(g0,g5) = 4.5
    c: Distance(g2,g0) = 5
    c: Distance(g1,g6) = 4.5
    c: Tangent(g14,g18) = -1.5708
    c: Tangent(g14,g19) = -1.5708
    c: Tangent(g15,g19) = -1.5708
    c: Tangent(g15,g20) = -1.5708
    c: Tangent(g16,g20) = -1.5708
    c: Tangent(g16,g21) = -1.5708
    c: Tangent(g17,g21) = -1.5708
    c: Tangent(g17,g18) = -1.5708
    c: Vertical(g14)
    c: Vertical(g16)
    c: Horizontal(g15)
    c: Horizontal(g17)
    c: Equal(g18,g19)
    c: Equal(g19,g20)
    c: Equal(g20,g21)
    c: PointOnObject(g22,g14)
    c: PointOnObject(g22,g17)
    c: PointOnObject(g23,g15)
    c: PointOnObject(g23,g16)
    c: Radius(g19) = 6
    c: Equal(g15,g16)
    c: PointOnObject(g15,g-1)
    c: PointOnObject(g14,g-2)
    c: Distance(g0,g16) = 4.5
    c: DistanceY(g17) = 66
    c: DistanceY(g7) = 128
    c: Distance(g3,g2) = 5
    c: DistanceX(g2,g3) = 62
    c: DistanceX(g3) = 95
    c: DistanceX(g2) = 33
    c: Tangent(g24,g28) = -1.5708
    c: Tangent(g24,g29) = -1.5708
    c: Tangent(g25,g29) = -1.5708
    c: Tangent(g25,g30) = -1.5708
    c: Tangent(g26,g30) = -1.5708
    c: Tangent(g26,g31) = -1.5708
    c: Tangent(g27,g31) = -1.5708
    c: Tangent(g27,g28) = -1.5708
    c: Vertical(g24)
    c: Vertical(g26)
    c: Horizontal(g25)
    c: Horizontal(g27)
    c: Equal(g28,g29)
    c: Equal(g29,g30)
    c: Equal(g30,g31)
    c: PointOnObject(g32,g24)
    c: PointOnObject(g32,g27)
    c: PointOnObject(g33,g25)
    c: PointOnObject(g33,g26)
    c: Radius(g29) = 6
    c: PointOnObject(g25,g-1)
    c: PointOnObject(g24,g-2)
    c: Equal(g34,g2)
    c: Vertical(g2,g34)
    c: Horizontal(g1,g35)
    c: Distance(g2,g34) = 5
    c: Distance(g35,g1) = 5
    c: Equal(g25,g26)
    c: Equal(g35,g1)
    c: Distance(g35,g26) = 4.5
    c: DistanceY(g27) = 190
    c: DistanceX(g35) = 157
FEATURE [PartDesign::Body] Body001  label="Templates"
  AllowCompound = false
  Group = -> [Sketch003,Sketch004,Sketch006]
  Origin = -> Origin001
FEATURE [Part::Part2DObjectPython] Wire001  # Draft 2D object (typed FeaturePython)
  Area = 146.221
  ChamferSize = 0
  Closed = true
  End = (0,0,-18)
  FilletRadius = 0
  Length = 137.05
  MakeFace = true
  Placement = pos=(0,0,0) rot=(1,0,0;1.5708rad)
  Points = (19) [(0,0,0),(-2,-2,-4.44089e-16),(-2,-17,-3.77476e-15),(-3,-18,-3.9968e-15),(-10,-18,-3.9968e-15),(-12,-20,-4.44089e-15),(-12,-29,-6.43929e-15),+12 more]
  Start = (0,0,0)
  Subdivisions = 0
FEATURE [Part::Part2DObjectPython] Wire002  # Draft 2D object (typed FeaturePython)
  Area = 15
  ChamferSize = 0
  Closed = true
  End = (-10,0,-29)
  FilletRadius = 0
  Length = 25.2611
  MakeFace = true
  Placement = pos=(-10,0,-27) rot=(1,0,0;1.5708rad)
  Points = (4) [(0,0,0),(6,7,1.55431e-15),(8,7,1.55431e-15),(0,-2,-4.44089e-16)]
  Start = (-10,0,-27)
  Subdivisions = 0
FEATURE [Part::Part2DObjectPython] Wire003  # Draft 2D object (typed FeaturePython)
  Area = 2
  ChamferSize = 0
  Closed = true
  End = (0,0,-4)
  FilletRadius = 0
  Length = 6.82843
  MakeFace = true
  Placement = pos=(0,0,-2) rot=(1,0,0;1.5708rad)
  Points = (3) [(0,0,0),(2,0,0),(0,-2,-4.44089e-16)]
  Start = (0,0,-2)
  Subdivisions = 0
note: 3 file-system paths scrubbed to <path> (originals preserved in the JSON sidecar)
